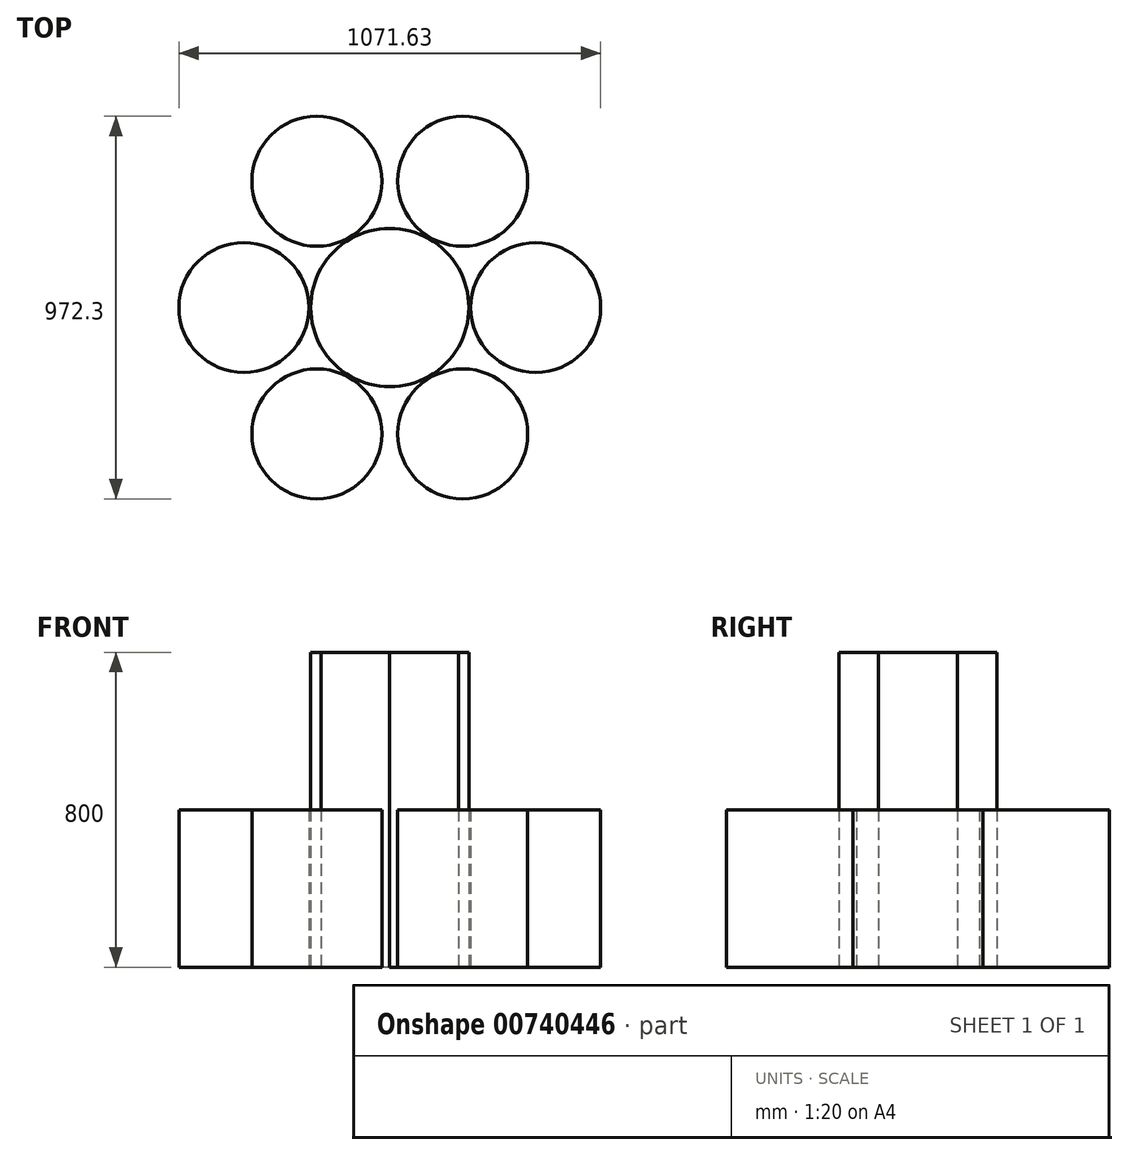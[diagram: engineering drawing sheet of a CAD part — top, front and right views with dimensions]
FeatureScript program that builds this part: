
annotation { "Feature Type Name" : "Feature", "Feature Type Description" : "" }
export const myFeature = defineFeature(function(context is Context, id is Id, definition is map)
    precondition{}
    {
        {
            var Q0;
            Q0=qCreatedBy(makeId("Top.planeOp"),FACE);
            var sketch = newSketch(context, id + "F0", { "sketchPlane" : qUnion([Q0])});
            skCircle(sketch, "E0", {"center": v(0, 0) * mm, "radius": 203.2 * mm});
            skCircle(sketch, "E1", {"center": v(-368.3, 0) * mm, "radius": 165.1 * mm});
            skCircle(sketch, "E2.1.0", {"center": v(1.2, 2.1) * mm, "radius": 203.2 * mm});
            skCircle(sketch, "E2.1.1", {"center": v(-182.94, 321.05) * mm, "radius": 165.1 * mm});
            skCircle(sketch, "E2.2.0", {"center": v(3.62, 2.1) * mm, "radius": 203.2 * mm});
            skCircle(sketch, "E2.2.1", {"center": v(187.77, 321.05) * mm, "radius": 165.1 * mm});
            skCircle(sketch, "E2.3.0", {"center": v(4.83, 0) * mm, "radius": 203.2 * mm});
            skCircle(sketch, "E2.3.1", {"center": v(373.13, 0) * mm, "radius": 165.1 * mm});
            skCircle(sketch, "E2.4.0", {"center": v(3.62, -2.1) * mm, "radius": 203.2 * mm});
            skCircle(sketch, "E2.4.1", {"center": v(187.77, -321.05) * mm, "radius": 165.1 * mm});
            skCircle(sketch, "E2.5.0", {"center": v(1.2, -2.1) * mm, "radius": 203.2 * mm});
            skCircle(sketch, "E2.5.1", {"center": v(-182.94, -321.05) * mm, "radius": 165.1 * mm});
            skPoint(sketch, "E2.center", {"position": v(2.41, 0) * mm});
            skLineSegment(sketch, "E2.anchor1", {"start": v(2.41, 0) * mm, "end": v(-368.3, 0) * mm, "construction": true});
            skLineSegment(sketch, "E2.anchor2", {"start": v(2.41, 0) * mm, "end": v(-182.94, -321.05) * mm, "construction": true});
            skSolve(sketch);
        }
        {
            var Q0;
            {var subQ5=sQuery(id+"F0.wireOp",EDGE,"E2.1.0");var subQ6=sQuery(id+"F0.wireOp",EDGE,"E0");var subQ7=makeQuery(id+"F0.imprint","INTERSECT",VERTEX,{"disambiguationData":[OD(1.0)],"derivedFrom":[subQ6,subQ5]});Q0=makeQuery(id+"F0.imprint","IMPRINT",FACE,{"disambiguationData":[TD([[makeQuery(id+"F0.imprint","IMPRINT",EDGE,{"disambiguationData":[TD([[subQ7,-1.0]])],"derivedFrom":subQ6}),1.0]])]});}
            extrude(context, id + "F1", {"entities" : qUnion([Q0]), "depth" : 800 * mm, "offsetDistance" : 25 * mm});
        }
        {
            var Q0;
            Q0=makeQuery(id+"F0.imprint","IMPRINT",FACE,{"disambiguationData":[TD([[makeQuery(id+"F0.imprint","IMPRINT",EDGE,{"derivedFrom":sQuery(id+"F0.wireOp",EDGE,"E1")}),1.0]])]});
            var Q1;
            Q1=makeQuery(id+"F0.imprint","IMPRINT",FACE,{"disambiguationData":[TD([[makeQuery(id+"F0.imprint","IMPRINT",EDGE,{"derivedFrom":sQuery(id+"F0.wireOp",EDGE,"E2.1.1")}),1.0]])]});
            var Q2;
            Q2=makeQuery(id+"F0.imprint","IMPRINT",FACE,{"disambiguationData":[TD([[makeQuery(id+"F0.imprint","IMPRINT",EDGE,{"derivedFrom":sQuery(id+"F0.wireOp",EDGE,"E2.2.1")}),1.0]])]});
            var Q3;
            Q3=makeQuery(id+"F0.imprint","IMPRINT",FACE,{"disambiguationData":[TD([[makeQuery(id+"F0.imprint","IMPRINT",EDGE,{"derivedFrom":sQuery(id+"F0.wireOp",EDGE,"E2.3.1")}),1.0]])]});
            var Q4;
            Q4=makeQuery(id+"F0.imprint","IMPRINT",FACE,{"disambiguationData":[TD([[makeQuery(id+"F0.imprint","IMPRINT",EDGE,{"derivedFrom":sQuery(id+"F0.wireOp",EDGE,"E2.4.1")}),1.0]])]});
            var Q5;
            Q5=makeQuery(id+"F0.imprint","IMPRINT",FACE,{"disambiguationData":[TD([[makeQuery(id+"F0.imprint","IMPRINT",EDGE,{"derivedFrom":sQuery(id+"F0.wireOp",EDGE,"E2.5.1")}),1.0]])]});
            extrude(context, id + "F2", {"entities" : qUnion([Q0, Q1, Q2, Q3, Q4, Q5]), "operationType" : NewBodyOperationType.ADD, "depth" : 400 * mm, "offsetDistance" : 25 * mm});
        }
    });
